# Revit family: ASH_ArmitageShanks_WallHungHandRinseBasins_Contour21-60cm_S2155
name_source: partatom
category: Plumbing Fixtures
revit_build: Autodesk Revit MEP 2012 (Build: 20110309_2315(x64)
units: mm (PartAtom-declared; Revit-internal decimal feet)

## types (1)
- S215501 - Contour 21 back outlet washbasin, 60cm, no tapholes, no overflow, no chainstay hole
    Accessories = www.idealspec.co.uk
    AreaUnits = millimeters
    Assembly Code = C1030200
    AssetType = Fixed
    BIMObjectName = ASH_ArmitageShanks_WallHungHandRinseBasins_Contour21_S2155
    BasinToUndersideSpout = 200 mm
    Brand = Armitage Shanks
    CWFU = 0
    Category = SanitaryTerminal_WASHHANDBASIN_UK
    Color = White
    ConnectionType = Plumbing
    Default Elevation = 800 mm  [stored 2.62467 ft]
    Description = Contour 21 back outlet washbasin, 60 cm, no tapholes, no overflow, no chainstay hole
    DrainSize = 32 mm
    DurationUnit = year
    ECA = No
    ExpectedLife = 30
    Features = Back outlet washbasin, 60 cm, no tapholes, no overflow, no chainstay hole
    Finish = White
    HWFU = 0
    IfcExportAs = IfcSanitaryTerminalType
    IfcExportType = WASHHANDBASIN
    InstallationInstructions = www.idealspec.co.uk/resources.html
    LinearUnits = millimeters
    ManufacturerURL = www.idealspec.co.uk
    Material = Vitreous china
    Model = S215501
    ModelNumber = S215501
    ModelReference = Contour 21 back outlet washbasin, 60 cm, no tapholes, no overflow, no chainstay hole
    NBSDescription = Health care clinical wash basins
    NBSReference = 45-35-70/361
    Name = WallHungHandRinseBasins_Contour21_S2155_ArmitageShanks
    NettWeight = 19.5 Kg
    NominalDepth = 480 mm  [stored 1.5748 ft]
    NominalHeight = 195 mm
    NominalLength = 480 mm  [stored 1.5748 ft]
    NominalWidth = 600 mm
    ProductInformation = www.idealspec.co.uk/assets/datasheet/S215501
    Shape = Sculptured
    Size = 600 x 480 x 195 mm
    Space = Internal
    SpareParts = www.fastpart-spares.co.uk
    URL = www.idealspec.co.uk
    Uniclass2 = Pr_40_20_96_35
    Version = 1
    VolumeUnits = Litres
    WFU = 0
    WRAS = No
    WarrantyDescription = Manufacturers warranty
    WarrantyDurationParts = 99
    WarrantyDurationUnit = year
    WashHandBasinMounting = Hospital
    WashHandBasinType = HANDRINSE
    WaterEfficientProduct = No

note: [stored X ft] marks values corroborated as IEEE doubles in the binary element streams (Revit-internal decimal feet)

## geometry (parser evidence)
native form markers: Sweep x9
no freeform markers — native parametric forms only
